# Revit family: Deckel_mit_Riffelblech_und_Drehriegel_Drehriegelabstand_500_mm
name_source: partatom
category: Generic Models
revit_build: Autodesk Revit 2015 (Build: 20140606_1530(x64)
units: mm (PartAtom-declared; Revit-internal decimal feet)

## types (6) — shared parameters
Manufacturer = OBO Bettermann
Material = Steel, Galvanized
Material2 = Aluminum 6061
URL = http://www.obo-bettermann.com

## per-type parameters (varying)
| type | "B" Dimension | GTIN | Manufacturer Art. No. |
| DF BKR10 FS AL | 100 mm  [stored 0.328084 ft] | 4012196146826 | 6049181 |
| DF BKR20 FS AL | 200 mm  [stored 0.656168 ft] | 4012196146857 | 6049183 |
| DF BKR30 FS AL | 300 mm | 4012196146864 | 6049185 |
| DF BKR40 FS AL | 400 mm  [stored 1.31234 ft] | 4012196146871 | 6049187 |
| DF BKR50 FS AL | 500 mm  [stored 1.64042 ft] | 4012196146888 | 6049189 |
| DF BKR60 FS AL | 600 mm | 4012196146918 | 6049191 |

note: column(s) folded — value = type name in every type: Article Type

note: [stored X ft] marks values corroborated as IEEE doubles in the binary element streams (Revit-internal decimal feet)

## geometry (parser evidence)
native form markers: Sweep x2
no freeform markers — native parametric forms only
